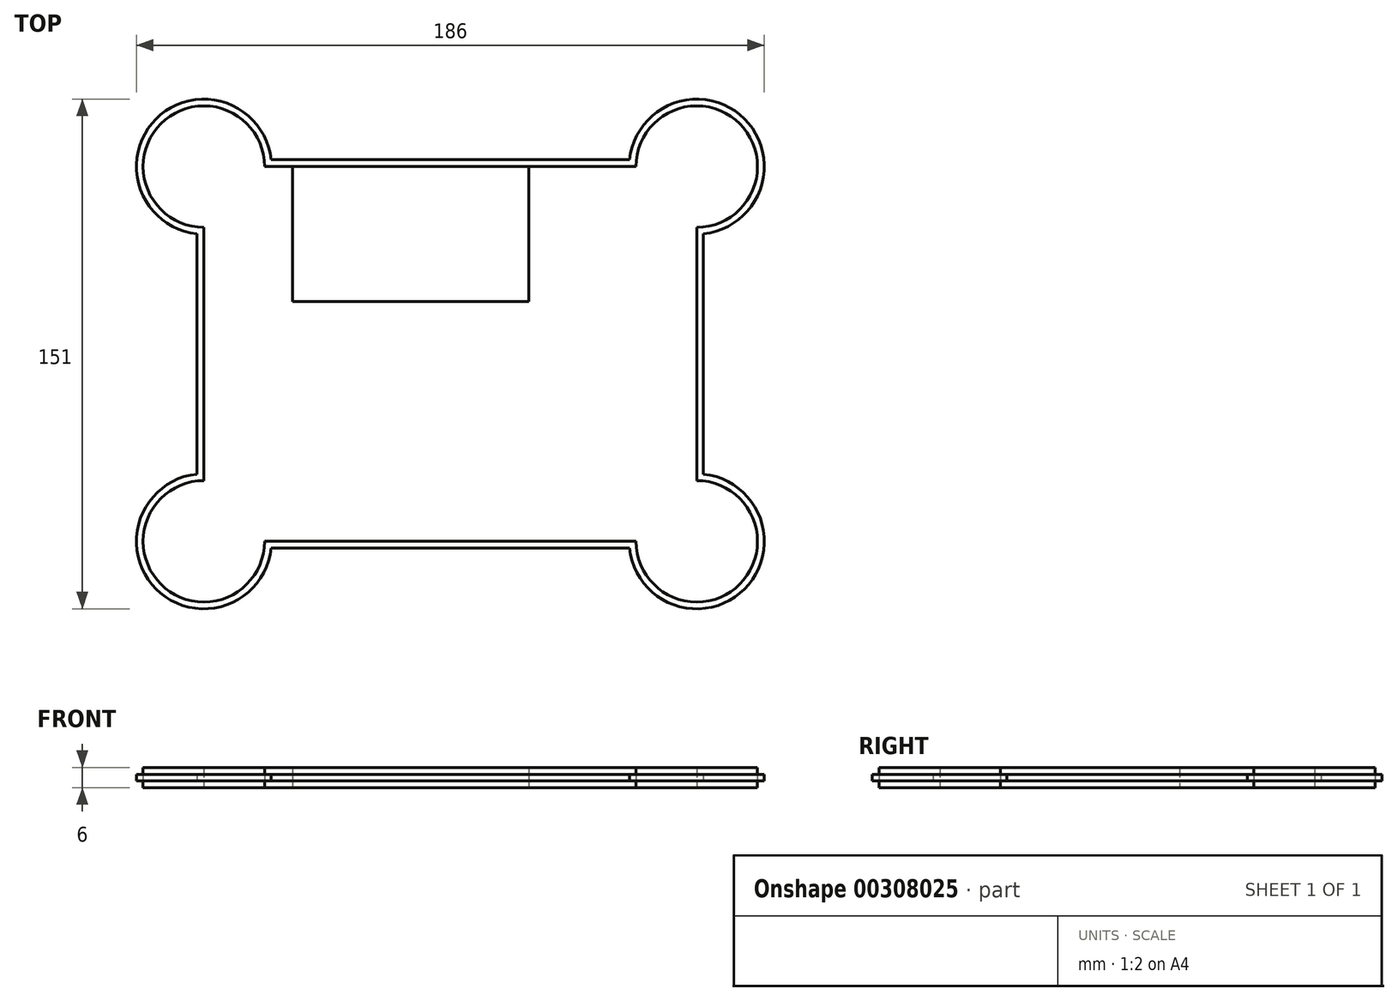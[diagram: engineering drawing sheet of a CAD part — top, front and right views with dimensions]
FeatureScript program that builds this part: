
annotation { "Feature Type Name" : "Feature", "Feature Type Description" : "" }
export const myFeature = defineFeature(function(context is Context, id is Id, definition is map)
    precondition{}
    {
        {
            var Q0;
            Q0=qCreatedBy(makeId("Top.planeOp"),FACE);
            var sketch = newSketch(context, id + "F0", { "sketchPlane" : qUnion([Q0])});
            skLineSegment(sketch, "E0.top", {"start": v(-53.1, 57.5) * mm, "end": v(53.1, 57.5) * mm});
            skLineSegment(sketch, "E0.left", {"start": v(-75, -35.6) * mm, "end": v(-75, 35.6) * mm});
            skPoint(sketch, "E0.middle", {"position": v(0, 0) * mm});
            skLineSegment(sketch, "E1.bottom", {"start": v(55, -55.5) * mm, "end": v(-55, -55.5) * mm});
            skLineSegment(sketch, "E1.top", {"start": v(55, 55.5) * mm, "end": v(-55, 55.5) * mm});
            skLineSegment(sketch, "E1.left", {"start": v(73, -37.5) * mm, "end": v(73, 37.5) * mm});
            skLineSegment(sketch, "E1.right", {"start": v(-73, -37.5) * mm, "end": v(-73, 37.5) * mm});
            skArc(sketch, "E2", {"start": v(-75, -35.6) * mm, "mid": v(-87.14, -69.64) * mm, "end": v(-53.1, -57.5) * mm});
            skArc(sketch, "E3", {"start": v(-73, -37.5) * mm, "mid": v(-85.73, -68.23) * mm, "end": v(-55, -55.5) * mm});
            skArc(sketch, "E4.MirrorC", {"start": v(75, -35.6) * mm, "mid": v(87.14, -69.64) * mm, "end": v(53.1, -57.5) * mm});
            skArc(sketch, "E5.MirrorC", {"start": v(73, -37.5) * mm, "mid": v(85.73, -68.23) * mm, "end": v(55, -55.5) * mm});
            skArc(sketch, "E6.MirrorC", {"start": v(-75, 35.6) * mm, "mid": v(-87.14, 69.64) * mm, "end": v(-53.1, 57.5) * mm});
            skArc(sketch, "E7.MirrorC", {"start": v(-73, 37.5) * mm, "mid": v(-85.73, 68.23) * mm, "end": v(-55, 55.5) * mm});
            skArc(sketch, "E8.MirrorC", {"start": v(73, 37.5) * mm, "mid": v(85.73, 68.23) * mm, "end": v(55, 55.5) * mm});
            skArc(sketch, "E9.MirrorC", {"start": v(75, 35.6) * mm, "mid": v(87.14, 69.64) * mm, "end": v(53.1, 57.5) * mm});
            skPoint(sketch, "E10.orphan", {"position": v(-75, 57.5) * mm});
            skPoint(sketch, "E11.trimOffspring.end.orphan", {"position": v(75, 57.5) * mm});
            skLineSegment(sketch, "E12.trimOffspring", {"start": v(75, -35.6) * mm, "end": v(75, 35.6) * mm});
            skPoint(sketch, "E13.orphan", {"position": v(75, -57.5) * mm});
            skLineSegment(sketch, "E14.trimOffspring", {"start": v(-53.1, -57.5) * mm, "end": v(53.1, -57.5) * mm});
            skPoint(sketch, "E15.orphan", {"position": v(-75, -57.5) * mm});
            skLineSegment(sketch, "E16", {"start": v(25, -57.5) * mm, "end": v(25, -55.5) * mm});
            skLineSegment(sketch, "E17", {"start": v(25, -55.5) * mm, "end": v(-25, -55.5) * mm});
            skLineSegment(sketch, "E18", {"start": v(-25, -55.5) * mm, "end": v(-25, -57.5) * mm});
            skLineSegment(sketch, "E19", {"start": v(-73, -55.5) * mm, "end": v(-73, -73.5) * mm});
            skLineSegment(sketch, "E20", {"start": v(-68, -74.86) * mm, "end": v(-68, -72.8) * mm});
            skLineSegment(sketch, "E21", {"start": v(-78, -72.8) * mm, "end": v(-78, -74.86) * mm});
            skLineSegment(sketch, "E22.MirrorCS", {"start": v(78, -72.8) * mm, "end": v(78, -74.86) * mm});
            skLineSegment(sketch, "E23.MirrorCS", {"start": v(68, -74.86) * mm, "end": v(68, -72.8) * mm});
            skLineSegment(sketch, "E24", {"start": v(-46.75, 55.5) * mm, "end": v(-46.75, 15.5) * mm});
            skLineSegment(sketch, "E25", {"start": v(-46.75, 15.5) * mm, "end": v(23.25, 15.5) * mm});
            skLineSegment(sketch, "E26", {"start": v(23.25, 15.5) * mm, "end": v(23.25, 55.5) * mm});
            skSolve(sketch);
        }
        {
            var Q0;
            Q0=qSketchRegion(id+"F0",true);
            var Q1;
            Q1=makeQuery(id+"F0.imprint","IMPRINT",FACE,{"disambiguationData":[TD([[makeQuery(id+"F0.imprint","IMPRINT",EDGE,{"derivedFrom":sQuery(id+"F0.wireOp",EDGE,"E1.top")}),1.0]])]});
            extrude(context, id + "F1", {"entities" : qUnion([Q0, Q1]), "depth" : 4 * mm});
        }
        {
            var Q0;
            {var subQ3=sQuery(id+"F0.wireOp",EDGE,"E18");Q0=makeQuery(id+"F0.imprint","IMPRINT",FACE,{"disambiguationData":[TD([[makeQuery(id+"F0.imprint","IMPRINT",EDGE,{"derivedFrom":subQ3}),-1.0]])]});}
            var Q1;
            {var subQ2=sQuery(id+"F0.wireOp",EDGE,"E20");Q1=makeQuery(id+"F0.imprint","IMPRINT",FACE,{"disambiguationData":[TD([[makeQuery(id+"F0.imprint","IMPRINT",EDGE,{"derivedFrom":subQ2}),1.0]])]});}
            var Q2;
            Q2=makeQuery(id+"F0.imprint","IMPRINT",FACE,{"disambiguationData":[TD([[makeQuery(id+"F0.imprint","IMPRINT",EDGE,{"derivedFrom":sQuery(id+"F0.wireOp",EDGE,"E0.top")}),-1.0]])]});
            var Q3;
            {var subQ0=sQuery(id+"F0.wireOp",EDGE,"E16");Q3=makeQuery(id+"F0.imprint","IMPRINT",FACE,{"disambiguationData":[TD([[makeQuery(id+"F0.imprint","IMPRINT",EDGE,{"derivedFrom":subQ0}),1.0]])]});}
            var Q4;
            {var subQ7=sQuery(id+"F0.wireOp",EDGE,"E16");Q4=makeQuery(id+"F0.imprint","IMPRINT",FACE,{"disambiguationData":[TD([[makeQuery(id+"F0.imprint","IMPRINT",EDGE,{"derivedFrom":subQ7}),-1.0]])]});}
            var Q5;
            {var subQ0=sQuery(id+"F0.wireOp",EDGE,"E22.MirrorCS");Q5=makeQuery(id+"F0.imprint","IMPRINT",FACE,{"disambiguationData":[TD([[makeQuery(id+"F0.imprint","IMPRINT",EDGE,{"derivedFrom":subQ0}),-1.0]])]});}
            extrude(context, id + "F2", {"entities" : qUnion([Q0, Q1, Q2, Q3, Q4, Q5]), "operationType" : NewBodyOperationType.REMOVE, "depth" : 2 * mm});
        }
        {
            var Q0;
            Q0=makeQuery(id+"F0.imprint","IMPRINT",FACE,{"disambiguationData":[TD([[makeQuery(id+"F0.imprint","IMPRINT",EDGE,{"derivedFrom":sQuery(id+"F0.wireOp",EDGE,"E1.top")}),1.0]])]});
            extrude(context, id + "F3", {"entities" : qUnion([Q0]), "depth" : 6 * mm});
        }
        {
            var Q0;
            {var subQ0=sQuery(id+"F0.wireOp",EDGE,"E24");Q0=makeQuery(id+"F0.imprint","IMPRINT",FACE,{"disambiguationData":[TD([[makeQuery(id+"F0.imprint","IMPRINT",EDGE,{"derivedFrom":subQ0}),1.0]])]});}
            extrude(context, id + "F4", {"entities" : qUnion([Q0]), "operationType" : NewBodyOperationType.REMOVE, "depth" : 6 * mm});
        }
    });
